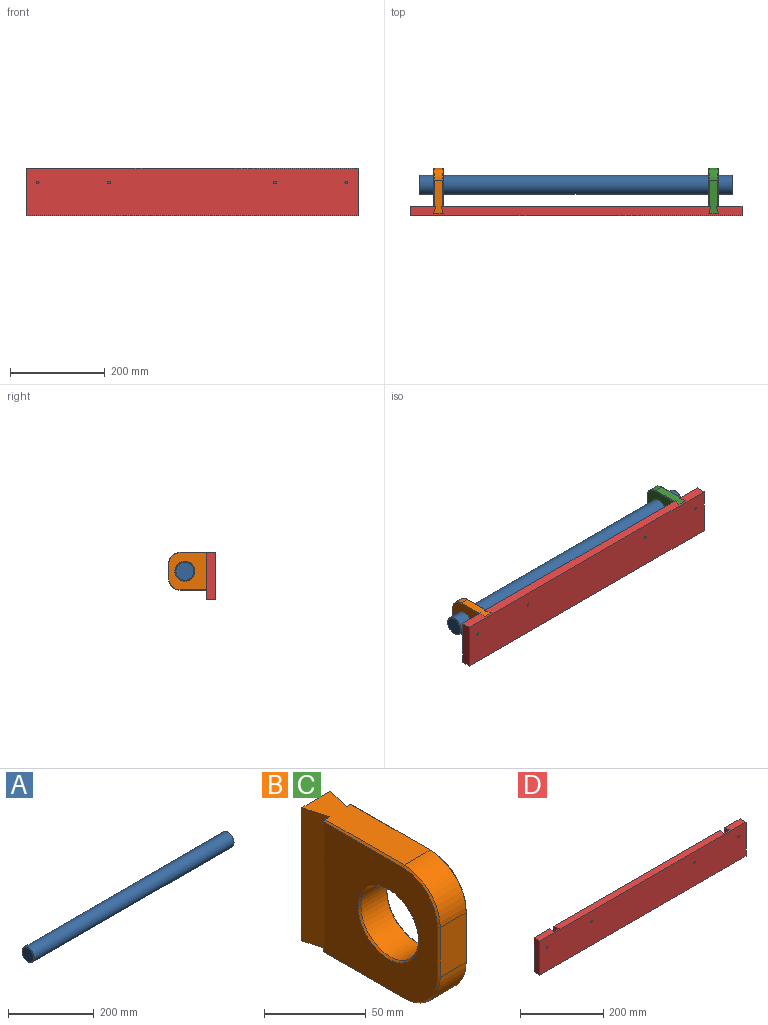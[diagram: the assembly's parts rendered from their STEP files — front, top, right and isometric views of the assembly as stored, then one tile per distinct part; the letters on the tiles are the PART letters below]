
ASSEMBLY  parts=4 mates=3
PART A: 5 faces, bbox 660x40x40 mm
  f0: plane 38x38mm, normal (-1,0,0), area 1134.1mm2, adj f3
  f1: plane 38x38mm, normal (1,0,0), area 1134.1mm2, adj f4
  f2: cylinder r=20mm len=658mm, axis (-1,0,0), area 82686.7mm2, adj f3,f4
  f3: cone r=19mm half-angle=45deg, axis (1,0,0), area 173.3mm2, adj f0,f2
  f4: cone r=20mm half-angle=45deg, axis (-1,0,0), area 173.3mm2, adj f1,f2
PART B: 25 faces, bbox 20x95x80 mm
  f0: plane 70x20mm, normal (0,0,-1), area 1229.7mm2, adj f5,f7,f8,f9,f10,f11,f17,f22
  f1: plane 70x20mm, normal (0,0,1), area 1229.7mm2, adj f5,f7,f8,f9,f10,f12,f13,f18
  f2: plane 79x78mm, normal (1,0,0), area 4529.3mm2, adj f10,f18,f19,f20,f21,f22,f24
  f3: plane 79x78mm, normal (-1,0,0), area 4529.3mm2, adj f8,f13,f14,f15,f16,f17,f23
  f4: plane 30x18mm, normal (0,-1,0), area 540mm2, adj f11,f12,f15,f20
  f5: plane 80x20mm, normal (0,1,0), area 1600mm2, adj f0,f1,f7,f9
  f6: cylinder r=20mm len=40mm, axis (1,0,0), area 2261.9mm2, adj f23,f24
  f7: plane 80x15mm, normal (-0.97,-0.26,0), area 1242.3mm2, adj f0,f1,f5,f8
  f8: plane 80x4.02mm, normal (0,1,0), area 320.5mm2, adj f0,f1,f3,f7,f13,f17
  f9: plane 80x15mm, normal (0.97,-0.26,0), area 1242.3mm2, adj f0,f1,f5,f10
  f10: plane 80x4.02mm, normal (0,1,0), area 320.5mm2, adj f0,f1,f2,f9,f18,f22
  f11: cylinder r=25mm len=25mm, axis (1,0,0), area 706.9mm2, adj f0,f4,f16,f21
  f12: cylinder r=25mm len=25mm, axis (-1,0,0), area 706.9mm2, adj f1,f4,f14,f19
  f13: plane 55x1mm, normal (-0.71,0,0.71), area 77.8mm2, adj f1,f3,f8,f14
  f14: cone r=24mm half-angle=45deg, axis (1,0,0), area 54.4mm2, adj f3,f12,f13,f15
  f15: plane 30x1mm, normal (-0.71,-0.71,0), area 42.4mm2, adj f3,f4,f14,f16
  f16: cone r=24mm half-angle=45deg, axis (1,0,0), area 54.4mm2, adj f3,f11,f15,f17
  f17: plane 55x1mm, normal (-0.71,0,-0.71), area 77.8mm2, adj f0,f3,f8,f16
  f18: plane 55x1mm, normal (0.71,0,0.71), area 77.8mm2, adj f1,f2,f10,f19
  f19: cone r=24mm half-angle=45deg, axis (-1,0,0), area 54.4mm2, adj f2,f12,f18,f20
  f20: plane 30x1mm, normal (0.71,-0.71,0), area 42.4mm2, adj f2,f4,f19,f21
  f21: cone r=24mm half-angle=45deg, axis (-1,0,0), area 54.4mm2, adj f2,f11,f20,f22
  f22: plane 55x1mm, normal (0.71,0,-0.71), area 77.8mm2, adj f0,f2,f10,f21
  f23: cone r=21mm half-angle=45deg, axis (-1,0,0), area 182.2mm2, adj f3,f6
  f24: cone r=20mm half-angle=45deg, axis (1,0,0), area 182.2mm2, adj f2,f6
PART C: same geometry as B
PART D: 22 faces, bbox 700x20x100 mm
  f0: plane 700x100mm, normal (0,-1,0), area 69921.5mm2, adj f2,f3,f4,f5,f14,f15,f16,f17
  f1: plane 700x100mm, normal (0,1,0), area 67831.7mm2, adj f2,f3,f4,f5,f6,f8,f9,f10
  f2: plane 700x20mm, normal (0,0,1), area 13520.6mm2, adj f0,f1,f3,f4,f6,f7,f8,f10
  f3: plane 100x20mm, normal (1,0,0), area 2000mm2, adj f0,f1,f2,f5
  f4: plane 100x20mm, normal (-1,0,0), area 2000mm2, adj f0,f1,f2,f5
  f5: plane 700x20mm, normal (0,0,-1), area 14000mm2, adj f0,f1,f3,f4
  f6: plane 80x15mm, normal (0.97,-0.26,0), area 1242.3mm2, adj f1,f2,f7,f9
  f7: plane 80x20mm, normal (0,1,0), area 1600mm2, adj f2,f6,f8,f9
  f8: plane 80x15mm, normal (-0.97,-0.26,0), area 1242.3mm2, adj f1,f2,f7,f9
  f9: plane 20x15mm, normal (0,0,1), area 239.7mm2, adj f1,f6,f7,f8
  f10: plane 80x15mm, normal (-0.97,-0.26,0), area 1242.3mm2, adj f1,f2,f12,f13
  f11: plane 80x15mm, normal (0.97,-0.26,0), area 1242.3mm2, adj f1,f2,f12,f13
  f12: plane 80x20mm, normal (0,1,0), area 1600mm2, adj f2,f10,f11,f13
  f13: plane 20x15mm, normal (0,0,1), area 239.7mm2, adj f1,f10,f11,f12
  f14: cylinder r=2.5mm len=18mm, axis (0,1,0), area 282.7mm2, adj f0,f18
  f15: cylinder r=2.5mm len=18mm, axis (0,1,0), area 282.7mm2, adj f0,f19
  f16: cylinder r=2.5mm len=18mm, axis (0,1,0), area 282.7mm2, adj f0,f20
  f17: cylinder r=2.5mm len=18mm, axis (0,1,0), area 282.7mm2, adj f0,f21
  f18: cone r=4.5mm half-angle=45deg, axis (0,1,0), area 62.2mm2, adj f1,f14
  f19: cone r=4.5mm half-angle=45deg, axis (0,1,0), area 62.2mm2, adj f1,f15
  f20: cone r=2.5mm half-angle=45deg, axis (0,1,0), area 62.2mm2, adj f1,f16
  f21: cone r=2.5mm half-angle=45deg, axis (0,1,0), area 62.2mm2, adj f1,f17
PLACE A rot(axis=(1,0,0),90deg) t=(-137.54,154.8,-44.07)mm
PLACE B rot(axis=(0,0,-1),180deg) t=(-87.54,189.8,-84.07)mm
PLACE C rot(axis=(0,0,-1),180deg) t=(492.46,189.8,-84.07)mm
PLACE D rot(axis=(-0.51,0.35,0.78),0deg) t=(-197.54,9.8,-104.07)mm
MATE slider B.f0 <-> D.f13  axis (0,0,-1) through (-97.54,94.8,-84.07)mm
MATE slider C.f0 <-> D.f9  axis (0,0,-1) through (482.46,94.8,-84.07)mm
MATE slider A.f2 <-> C.f6  axis (1,0,0) through (522.46,154.8,-44.07)mm
